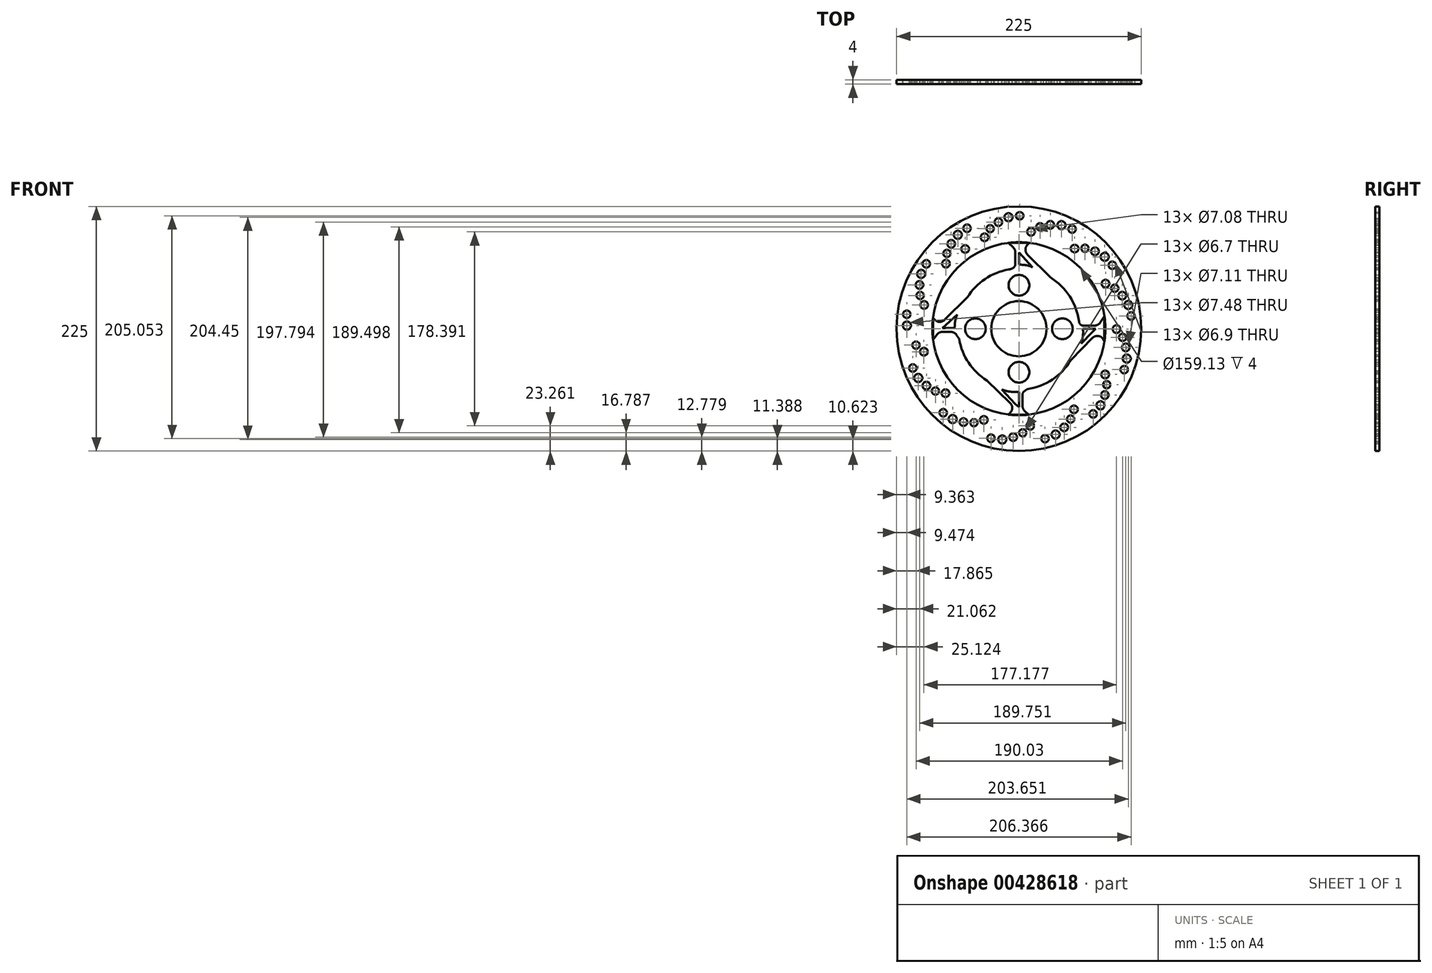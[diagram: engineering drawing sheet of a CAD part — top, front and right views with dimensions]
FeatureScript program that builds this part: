
annotation { "Feature Type Name" : "Feature", "Feature Type Description" : "" }
export const myFeature = defineFeature(function(context is Context, id is Id, definition is map)
    precondition{}
    {
        {
            var Q0;
            Q0=qCreatedBy(makeId("Front.planeOp"),FACE);
            var sketch = newSketch(context, id + "F0", { "sketchPlane" : qUnion([Q0])});
            skCircle(sketch, "E0", {"center": v(0.05, 0) * mm, "radius": 112.5 * mm});
            skCircle(sketch, "E1", {"center": v(0.05, 0) * mm, "radius": 25.4 * mm});
            skCircle(sketch, "E2", {"center": v(-67.02, 59.85) * mm, "radius": 3.54 * mm});
            skCircle(sketch, "E3", {"center": v(-66.14, 69.28) * mm, "radius": 3.35 * mm});
            skCircle(sketch, "E4", {"center": v(-62.22, 78.1) * mm, "radius": 3.56 * mm});
            skCircle(sketch, "E5", {"center": v(-56.12, 86.39) * mm, "radius": 3.74 * mm});
            skCircle(sketch, "E6", {"center": v(-47.6, 92.4) * mm, "radius": 3.45 * mm});
            skCircle(sketch, "E7.1.0", {"center": v(-89.84, 50.41) * mm, "radius": 3.74 * mm});
            skCircle(sketch, "E7.1.1", {"center": v(-91.39, 40.25) * mm, "radius": 3.56 * mm});
            skCircle(sketch, "E7.1.2", {"center": v(-90.76, 30.6) * mm, "radius": 3.35 * mm});
            skCircle(sketch, "E7.1.3", {"center": v(-87.15, 21.85) * mm, "radius": 3.54 * mm});
            skCircle(sketch, "E7.1.4", {"center": v(-85.09, 59.7) * mm, "radius": 3.45 * mm});
            skCircle(sketch, "E7.2.0", {"center": v(-102.98, 2.89) * mm, "radius": 3.74 * mm});
            skCircle(sketch, "E7.2.1", {"center": v(-49.31, 73.37) * mm, "radius": 3.56 * mm});
            skCircle(sketch, "E7.2.2", {"center": v(-94.58, -15.08) * mm, "radius": 3.35 * mm});
            skCircle(sketch, "E7.2.3", {"center": v(-87.33, -21.15) * mm, "radius": 3.54 * mm});
            skCircle(sketch, "E7.2.4", {"center": v(-103.09, 13.32) * mm, "radius": 3.45 * mm});
            skCircle(sketch, "E7.3.0", {"center": v(-92.52, -45.3) * mm, "radius": 3.74 * mm});
            skCircle(sketch, "E7.3.1", {"center": v(-85.04, -52.35) * mm, "radius": 3.56 * mm});
            skCircle(sketch, "E7.3.2", {"center": v(-76.74, -57.3) * mm, "radius": 3.35 * mm});
            skCircle(sketch, "E7.3.3", {"center": v(-67.5, -59.31) * mm, "radius": 3.54 * mm});
            skCircle(sketch, "E7.3.4", {"center": v(-97.47, -36.11) * mm, "radius": 3.45 * mm});
            skCircle(sketch, "E7.4.0", {"center": v(-60.87, -83.1) * mm, "radius": 3.74 * mm});
            skCircle(sketch, "E7.4.1", {"center": v(-50.97, -85.87) * mm, "radius": 3.56 * mm});
            skCircle(sketch, "E7.4.2", {"center": v(-41.32, -86.4) * mm, "radius": 3.35 * mm});
            skCircle(sketch, "E7.4.3", {"center": v(-32.2, -83.88) * mm, "radius": 3.54 * mm});
            skCircle(sketch, "E7.4.4", {"center": v(-69.52, -77.27) * mm, "radius": 3.45 * mm});
            skCircle(sketch, "E7.5.0", {"center": v(-15.28, -101.88) * mm, "radius": 3.74 * mm});
            skCircle(sketch, "E7.5.1", {"center": v(-5.23, -99.72) * mm, "radius": 3.56 * mm});
            skCircle(sketch, "E7.5.2", {"center": v(3.57, -95.71) * mm, "radius": 3.35 * mm});
            skCircle(sketch, "E7.5.3", {"center": v(10.47, -89.24) * mm, "radius": 3.54 * mm});
            skCircle(sketch, "E7.5.4", {"center": v(-25.65, -100.73) * mm, "radius": 3.45 * mm});
            skCircle(sketch, "E7.6.0", {"center": v(33.81, -97.3) * mm, "radius": 3.74 * mm});
            skCircle(sketch, "E7.6.1", {"center": v(41.72, -90.73) * mm, "radius": 3.56 * mm});
            skCircle(sketch, "E7.6.2", {"center": v(47.64, -83.1) * mm, "radius": 3.35 * mm});
            skCircle(sketch, "E7.6.3", {"center": v(50.74, -74.15) * mm, "radius": 3.54 * mm});
            skCircle(sketch, "E7.6.4", {"center": v(24.1, -101.11) * mm, "radius": 3.45 * mm});
            skCircle(sketch, "E7.7.0", {"center": v(75.16, -70.45) * mm, "radius": 3.74 * mm});
            skCircle(sketch, "E7.7.1", {"center": v(79.1, -60.95) * mm, "radius": 3.56 * mm});
            skCircle(sketch, "E7.7.2", {"center": v(80.8, -51.43) * mm, "radius": 3.35 * mm});
            skCircle(sketch, "E7.7.3", {"center": v(79.4, -42.08) * mm, "radius": 3.54 * mm});
            skCircle(sketch, "E7.7.4", {"center": v(68.33, -78.33) * mm, "radius": 3.45 * mm});
            skCircle(sketch, "E7.8.0", {"center": v(99.3, -27.45) * mm, "radius": 3.74 * mm});
            skCircle(sketch, "E7.8.1", {"center": v(98.36, -17.2) * mm, "radius": 3.56 * mm});
            skCircle(sketch, "E7.8.2", {"center": v(95.45, -8) * mm, "radius": 3.35 * mm});
            skCircle(sketch, "E7.8.3", {"center": v(89.85, -0.36) * mm, "radius": 3.54 * mm});
            skCircle(sketch, "E7.8.4", {"center": v(96.9, -37.6) * mm, "radius": 3.45 * mm});
            skCircle(sketch, "E7.9.0", {"center": v(100.67, 21.84) * mm, "radius": 3.74 * mm});
            skCircle(sketch, "E7.9.1", {"center": v(95.1, 30.48) * mm, "radius": 3.56 * mm});
            skCircle(sketch, "E7.9.2", {"center": v(88.23, 37.28) * mm, "radius": 3.35 * mm});
            skCircle(sketch, "E7.9.3", {"center": v(79.73, 41.44) * mm, "radius": 3.54 * mm});
            skCircle(sketch, "E7.9.4", {"center": v(103.28, 11.74) * mm, "radius": 3.45 * mm});
            skCircle(sketch, "E7.10.0", {"center": v(79, 66.12) * mm, "radius": 3.74 * mm});
            skCircle(sketch, "E7.10.1", {"center": v(70.04, 71.18) * mm, "radius": 3.56 * mm});
            skCircle(sketch, "E7.10.2", {"center": v(60.8, 74) * mm, "radius": 3.35 * mm});
            skCircle(sketch, "E7.10.3", {"center": v(51.34, 73.74) * mm, "radius": 3.54 * mm});
            skCircle(sketch, "E7.10.4", {"center": v(86, 58.39) * mm, "radius": 3.45 * mm});
            skCircle(sketch, "E7.11.0", {"center": v(39.22, 95.26) * mm, "radius": 3.74 * mm});
            skCircle(sketch, "E7.11.1", {"center": v(28.94, 95.57) * mm, "radius": 3.56 * mm});
            skCircle(sketch, "E7.11.2", {"center": v(19.44, 93.79) * mm, "radius": 3.35 * mm});
            skCircle(sketch, "E7.11.3", {"center": v(11.19, 89.15) * mm, "radius": 3.54 * mm});
            skCircle(sketch, "E7.11.4", {"center": v(49.01, 91.66) * mm, "radius": 3.45 * mm});
            skCircle(sketch, "E7.12.0", {"center": v(-9.54, 102.57) * mm, "radius": 3.74 * mm});
            skCircle(sketch, "E7.12.1", {"center": v(-18.8, 98.07) * mm, "radius": 3.56 * mm});
            skCircle(sketch, "E7.12.2", {"center": v(-26.37, 92.08) * mm, "radius": 3.35 * mm});
            skCircle(sketch, "E7.12.3", {"center": v(-31.52, 84.14) * mm, "radius": 3.54 * mm});
            skCircle(sketch, "E7.12.4", {"center": v(0.8, 103.94) * mm, "radius": 3.45 * mm});
            skPoint(sketch, "E7.center", {"position": v(0, 0) * mm});
            skCircle(sketch, "E8", {"center": v(0.05, 0) * mm, "radius": 79.56 * mm});
            skLineSegment(sketch, "E9", {"start": v(3.35, -60.68) * mm, "end": v(3.35, -70.95) * mm});
            skPoint(sketch, "E10.center", {"position": v(0.07, -0.36) * mm});
            skLineSegment(sketch, "E11", {"start": v(-62.58, -2.92) * mm, "end": v(-70.28, -2.92) * mm});
            skCircle(sketch, "E12", {"center": v(0.07, -0.36) * mm, "radius": 55.66 * mm});
            skCircle(sketch, "E13", {"center": v(40.05, -0.04) * mm, "radius": 9.53 * mm});
            skCircle(sketch, "E14", {"center": v(0.11, -40.04) * mm, "radius": 9.53 * mm});
            skCircle(sketch, "E15", {"center": v(-39.95, -0.04) * mm, "radius": 9.53 * mm});
            skCircle(sketch, "E16", {"center": v(0.11, 39.97) * mm, "radius": 9.53 * mm});
            skLineSegment(sketch, "E17", {"start": v(-5.25, 74.8) * mm, "end": v(-9.66, 78.97) * mm});
            skLineSegment(sketch, "E18", {"start": v(8.1, 77.4) * mm, "end": v(9.76, 78.97) * mm});
            skLineSegment(sketch, "E19.2.0", {"start": v(5.34, -75.57) * mm, "end": v(9.3, -79.3) * mm});
            skLineSegment(sketch, "E19.2.1", {"start": v(-8.1, -77.4) * mm, "end": v(-10.11, -79.3) * mm});
            skPoint(sketch, "E19.center", {"position": v(-0.18, -0.17) * mm});
            skLineSegment(sketch, "E20", {"start": v(-77.87, 8.93) * mm, "end": v(-78.85, 10.28) * mm});
            skLineSegment(sketch, "E21", {"start": v(-75.43, -5.55) * mm, "end": v(-78.85, -10.28) * mm});
            skLineSegment(sketch, "E22", {"start": v(74.95, 5.72) * mm, "end": v(78.79, 11.42) * mm});
            skLineSegment(sketch, "E23", {"start": v(77.42, -9.4) * mm, "end": v(78.79, -11.42) * mm});
            skLineSegment(sketch, "E24", {"start": v(-8.03, -68.22) * mm, "end": v(-29.34, -47.62) * mm});
            skLineSegment(sketch, "E25", {"start": v(-68.26, 8.15) * mm, "end": v(-47.17, 29.08) * mm});
            skLineSegment(sketch, "E26", {"start": v(67.61, -8.51) * mm, "end": v(48.03, -28.6) * mm});
            skLineSegment(sketch, "E27", {"start": v(7.96, 68.3) * mm, "end": v(29, 47.18) * mm});
            skPoint(sketch, "E28.visualSharp", {"position": v(3.35, 72.93) * mm});
            skArc(sketch, "E28.filletArc", {"start": v(8.1, 77.4) * mm, "mid": v(6.1, 72.89) * mm, "end": v(7.96, 68.3) * mm});
            skPoint(sketch, "E29.visualSharp", {"position": v(73.06, -2.92) * mm});
            skArc(sketch, "E29.filletArc", {"start": v(77.42, -9.4) * mm, "mid": v(72.73, -6.62) * mm, "end": v(67.61, -8.51) * mm});
            skArc(sketch, "E30.filletArc", {"start": v(-8.1, -77.4) * mm, "mid": v(-6.1, -72.82) * mm, "end": v(-8.03, -68.22) * mm});
            skPoint(sketch, "E31.visualSharp", {"position": v(-73.52, 2.92) * mm});
            skArc(sketch, "E31.filletArc", {"start": v(-77.87, 8.93) * mm, "mid": v(-73.25, 6.33) * mm, "end": v(-68.26, 8.15) * mm});
            skPoint(sketch, "E32.newPointA", {"position": v(-73.52, -2.92) * mm});
            skArc(sketch, "E32.filletArc", {"start": v(-70.28, -2.92) * mm, "mid": v(-73.17, -3.62) * mm, "end": v(-75.43, -5.55) * mm});
            skPoint(sketch, "E33.newPointA", {"position": v(-3.25, 72.93) * mm});
            skArc(sketch, "E33.filletArc", {"start": v(-3.25, 70.19) * mm, "mid": v(-3.77, 72.7) * mm, "end": v(-5.25, 74.8) * mm});
            skPoint(sketch, "E34.newPointA", {"position": v(73.06, 2.92) * mm});
            skArc(sketch, "E34.filletArc", {"start": v(69.68, 2.92) * mm, "mid": v(72.67, 3.67) * mm, "end": v(74.95, 5.72) * mm});
            skPoint(sketch, "E35.newPointA", {"position": v(2.9, -73.27) * mm});
            skArc(sketch, "E35.filletArc", {"start": v(3.35, -70.95) * mm, "mid": v(3.87, -73.47) * mm, "end": v(5.34, -75.57) * mm});
            skFitSpline(sketch, "E36", {"points": [v(58.33, 2.92) * mm, v(55.28, 6.63) * mm], "startDerivative": vector(-4.27, 2.22) * mm, "endDerivative": vector(-2.44, 8.9) * mm});
            skFitSpline(sketch, "E37", {"points": [v(3.35, -58.8) * mm, v(7.65, -55.5) * mm], "startDerivative": vector(4.3, 3.35) * mm, "endDerivative": vector(4.3, 3.35) * mm});
            skFitSpline(sketch, "E38", {"points": [v(-59.15, -2.92) * mm, v(-54.84, -9.48) * mm], "startDerivative": vector(4.34, -6.56) * mm, "endDerivative": vector(4.34, -6.56) * mm});
            skFitSpline(sketch, "E39", {"points": [v(-3.25, 58.57) * mm, v(-9.5, 54.47) * mm], "startDerivative": vector(-2.49, -6.7) * mm, "endDerivative": vector(-10.96, -1.54) * mm});
            skArc(sketch, "E40.filletArc", {"start": v(4.85, -57.65) * mm, "mid": v(3.75, -58.98) * mm, "end": v(3.35, -60.68) * mm});
            skArc(sketch, "E41.filletArc", {"start": v(-57.27, -5.79) * mm, "mid": v(-59.56, -3.68) * mm, "end": v(-62.58, -2.92) * mm});
            skLineSegment(sketch, "E42", {"start": v(67.61, -3.33) * mm, "end": v(57.13, -14.09) * mm});
            skLineSegment(sketch, "E43", {"start": v(58.9, 0) * mm, "end": v(70.8, 0) * mm});
            skLineSegment(sketch, "E44", {"start": v(67.61, -3.33) * mm, "end": v(70.8, 0) * mm});
            skFitSpline(sketch, "E45", {"points": [v(58.9, 0) * mm, v(57.13, -14.57) * mm], "startDerivative": vector(1.64, -12.23) * mm, "endDerivative": vector(-5.49, -15.1) * mm});
            skLineSegment(sketch, "E46", {"start": v(-70.25, 0.5) * mm, "end": v(-56.64, 13.08) * mm});
            skFitSpline(sketch, "E47", {"points": [v(-56.64, 13.08) * mm, v(-59.15, 0.5) * mm], "startDerivative": vector(-7.42, -16.98) * mm, "endDerivative": vector(-1.56, -14.2) * mm});
            skLineSegment(sketch, "E48", {"start": v(-70.25, 0.5) * mm, "end": v(-59.15, 0.5) * mm});
            skLineSegment(sketch, "E49", {"start": v(-3.25, -69.38) * mm, "end": v(-15.83, -55.77) * mm});
            skFitSpline(sketch, "E50", {"points": [v(-15.83, -55.77) * mm, v(-3.25, -58.28) * mm], "startDerivative": vector(16.98, -7.42) * mm, "endDerivative": vector(14.2, -1.56) * mm});
            skLineSegment(sketch, "E51", {"start": v(-3.25, -69.38) * mm, "end": v(0.05, -72.24) * mm});
            skLineSegment(sketch, "E52", {"start": v(-3.25, -58.28) * mm, "end": v(0.05, -58.28) * mm});
            skLineSegment(sketch, "E53", {"start": v(-3.25, 70.19) * mm, "end": v(-3.25, 58.57) * mm});
            skLineSegment(sketch, "E54", {"start": v(58.33, 2.92) * mm, "end": v(69.68, 2.92) * mm});
            skLineSegment(sketch, "E55", {"start": v(0.05, 70.19) * mm, "end": v(12.63, 56.58) * mm});
            skFitSpline(sketch, "E56", {"points": [v(12.63, 56.58) * mm, v(0.05, 59.09) * mm], "startDerivative": vector(-16.98, 7.42) * mm, "endDerivative": vector(-14.2, 1.56) * mm});
            skLineSegment(sketch, "E57", {"start": v(0.05, 70.19) * mm, "end": v(0.05, 59.09) * mm});
            skLineSegment(sketch, "E58", {"start": v(0.05, -58.28) * mm, "end": v(0.05, -72.24) * mm});
            skLineSegment(sketch, "E59", {"start": v(8.98, -79) * mm, "end": v(-9.67, -78.9) * mm});
            skLineSegment(sketch, "E60", {"start": v(-78.78, 10.18) * mm, "end": v(-78.78, -10.19) * mm});
            skLineSegment(sketch, "E61", {"start": v(-9.59, 78.9) * mm, "end": v(9.69, 78.9) * mm});
            skLineSegment(sketch, "E62", {"start": v(78.73, 11.33) * mm, "end": v(78.73, -11.33) * mm});
            skSolve(sketch);
        }
        {
            var Q0;
            Q0=makeQuery(id+"F0.imprint","IMPRINT",FACE,{"disambiguationData":[TD([[makeQuery(id+"F0.imprint","IMPRINT",EDGE,{"derivedFrom":sQuery(id+"F0.wireOp",EDGE,"E0")}),1.0]])]});
            extrude(context, id + "F1", {"entities" : qUnion([Q0]), "endBound" : BoundingType.SYMMETRIC, "depth" : 4 * mm});
        }
        {
            var Q0;
            Q0=makeQuery(id+"F0.imprint","IMPRINT",FACE,{"disambiguationData":[TD([[makeQuery(id+"F0.imprint","IMPRINT",EDGE,{"derivedFrom":sQuery(id+"F0.wireOp",EDGE,"E1")}),-1.0]])]});
            var Q1;
            {var subQ8=sQuery(id+"F0.wireOp",EDGE,"E27");Q1=makeQuery(id+"F0.imprint","IMPRINT",FACE,{"disambiguationData":[TD([[makeQuery(id+"F0.imprint","IMPRINT",EDGE,{"derivedFrom":subQ8}),-1.0]])]});}
            var Q2;
            {var subQ10=sQuery(id+"F0.wireOp",EDGE,"E26");Q2=makeQuery(id+"F0.imprint","IMPRINT",FACE,{"disambiguationData":[TD([[makeQuery(id+"F0.imprint","IMPRINT",EDGE,{"derivedFrom":subQ10}),-1.0]])]});}
            var Q3;
            Q3=makeQuery(id+"F0.imprint","IMPRINT",FACE,{"disambiguationData":[TD([[makeQuery(id+"F0.imprint","IMPRINT",EDGE,{"derivedFrom":sQuery(id+"F0.wireOp",EDGE,"E9")}),-1.0]])]});
            var Q4;
            Q4=makeQuery(id+"F0.imprint","IMPRINT",FACE,{"disambiguationData":[TD([[makeQuery(id+"F0.imprint","IMPRINT",EDGE,{"derivedFrom":sQuery(id+"F0.wireOp",EDGE,"E11")}),-1.0]])]});
            extrude(context, id + "F2", {"entities" : qUnion([Q0, Q1, Q2, Q3, Q4]), "operationType" : NewBodyOperationType.ADD, "endBound" : BoundingType.SYMMETRIC, "depth" : 4 * mm});
        }
        {
            var Q0;
            {var subQ5=sQuery(id+"F0.wireOp",EDGE,"E61");Q0=makeQuery(id+"F0.imprint","IMPRINT",FACE,{"disambiguationData":[TD([[makeQuery(id+"F0.imprint","IMPRINT",EDGE,{"derivedFrom":subQ5}),1.0]])]});}
            var Q1;
            {var subQ5=sQuery(id+"F0.wireOp",EDGE,"E62");Q1=makeQuery(id+"F0.imprint","IMPRINT",FACE,{"disambiguationData":[TD([[makeQuery(id+"F0.imprint","IMPRINT",EDGE,{"derivedFrom":subQ5}),1.0]])]});}
            var Q2;
            {var subQ5=sQuery(id+"F0.wireOp",EDGE,"E59");Q2=makeQuery(id+"F0.imprint","IMPRINT",FACE,{"disambiguationData":[TD([[makeQuery(id+"F0.imprint","IMPRINT",EDGE,{"derivedFrom":subQ5}),1.0]])]});}
            var Q3;
            {var subQ5=sQuery(id+"F0.wireOp",EDGE,"E60");Q3=makeQuery(id+"F0.imprint","IMPRINT",FACE,{"disambiguationData":[TD([[makeQuery(id+"F0.imprint","IMPRINT",EDGE,{"derivedFrom":subQ5}),-1.0]])]});}
            extrude(context, id + "F3", {"entities" : qUnion([Q0, Q1, Q2, Q3]), "endBound" : BoundingType.SYMMETRIC, "depth" : 4 * mm});
        }
    });
